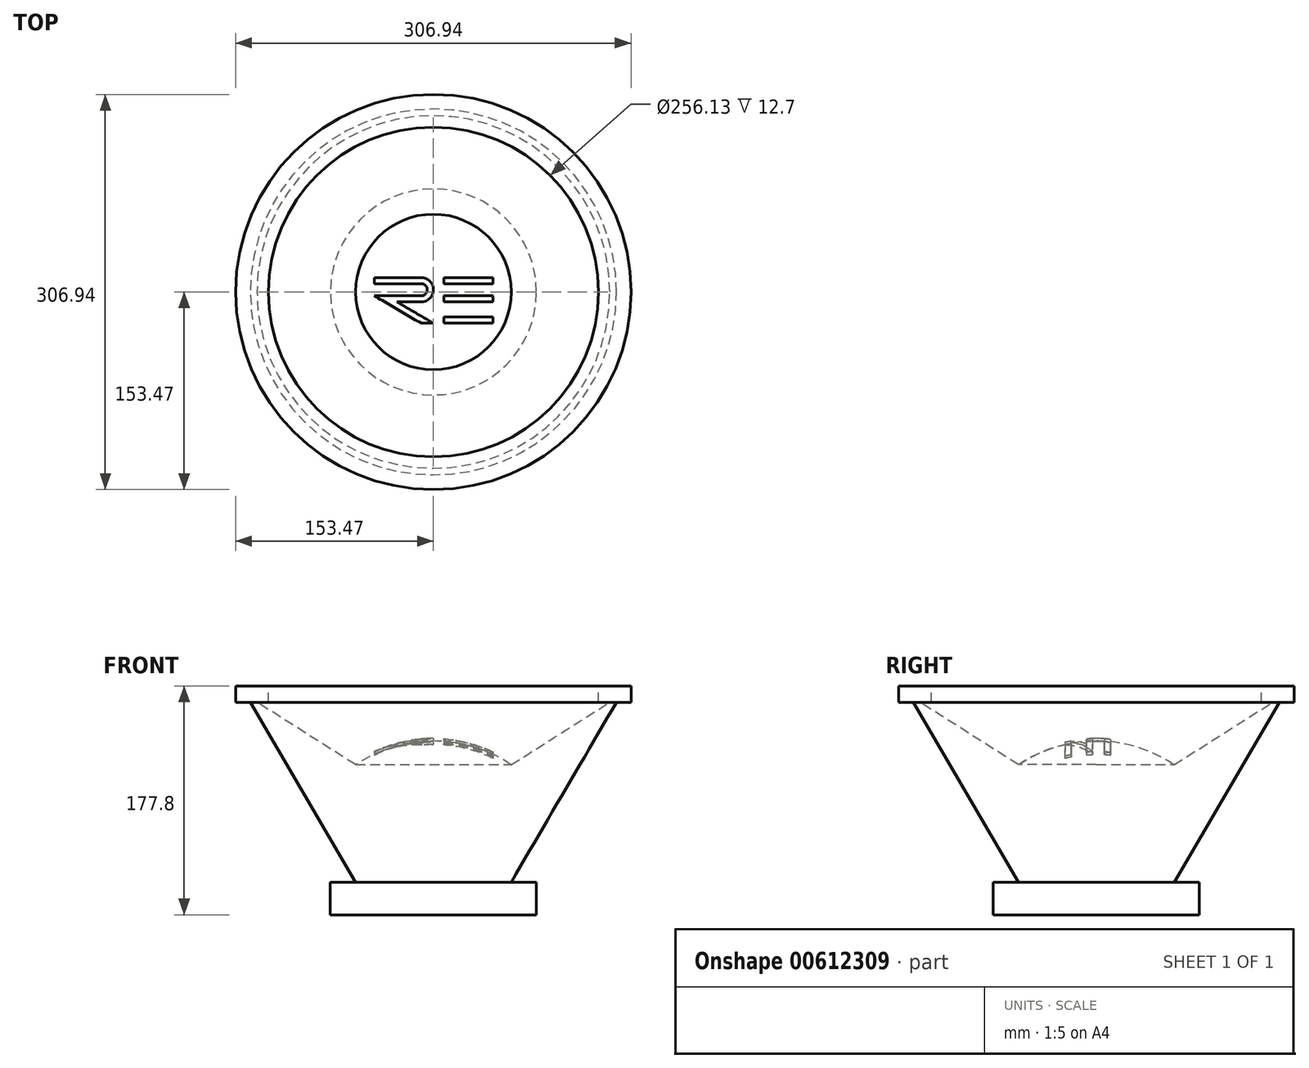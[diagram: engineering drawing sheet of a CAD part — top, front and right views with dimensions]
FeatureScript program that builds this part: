
annotation { "Feature Type Name" : "Feature", "Feature Type Description" : "" }
export const myFeature = defineFeature(function(context is Context, id is Id, definition is map)
    precondition{}
    {
        {
            var Q0;
            Q0=qCreatedBy(makeId("Right.planeOp"),FACE);
            var sketch = newSketch(context, id + "F0", { "sketchPlane" : qUnion([Q0])});
            skLineSegment(sketch, "E0", {"start": v(0, -91.62) * mm, "end": v(80.01, -91.62) * mm});
            skLineSegment(sketch, "E1", {"start": v(80.01, -91.62) * mm, "end": v(80.01, -66.22) * mm});
            skLineSegment(sketch, "E2", {"start": v(80.01, -66.22) * mm, "end": v(60.42, -66.22) * mm});
            skLineSegment(sketch, "E3", {"start": v(60.42, -66.22) * mm, "end": v(142.06, 73.48) * mm});
            skLineSegment(sketch, "E4", {"start": v(142.06, 73.48) * mm, "end": v(153.47, 73.48) * mm});
            skLineSegment(sketch, "E5", {"start": v(153.47, 73.48) * mm, "end": v(153.47, 86.18) * mm});
            skLineSegment(sketch, "E6", {"start": v(153.47, 86.18) * mm, "end": v(128.07, 86.18) * mm});
            skLineSegment(sketch, "E7", {"start": v(128.07, 86.18) * mm, "end": v(128.07, 73.48) * mm});
            skLineSegment(sketch, "E8", {"start": v(128.07, 73.48) * mm, "end": v(136.93, 73.48) * mm});
            skLineSegment(sketch, "E9", {"start": v(136.93, 73.48) * mm, "end": v(60.42, 24.96) * mm});
            skArc(sketch, "E10", {"start": v(60.42, 24.96) * mm, "mid": v(31.57, 38.63) * mm, "end": v(0, 43.39) * mm});
            skLineSegment(sketch, "E11", {"start": v(0, 43.39) * mm, "end": v(0, -91.62) * mm});
            skSolve(sketch);
        }
        {
            var Q0;
            Q0 = qSketchRegion(id + "F0", true);
            var Q1;
            Q1=sQuery(id+"F0.wireOp",EDGE,"E11");
            revolve(context, id + "F1", {"entities" : qUnion([Q0]), "axis" : qUnion([Q1]), "revolveType" : RevolveType.FULL});
        }
        {
            var Q0;
            Q0=qCreatedBy(makeId("Top.planeOp"),FACE);
            cPlane(context, id + "F2", {"entities" : qUnion([Q0]), "cplaneType" : CPlaneType.OFFSET, "offset" : 25.4 * mm, "width" : 152.4 * mm, "height" : 152.4 * mm});
        }
        {
            var Q0;
            Q0=qCreatedBy(id+"F2.planeOp",FACE);
            var sketch = newSketch(context, id + "F3", { "sketchPlane" : qUnion([Q0])});
            skLineSegment(sketch, "E12", {"start": v(-45.92, 11.17) * mm, "end": v(-9.42, 11.17) * mm});
            skArc(sketch, "E13", {"start": v(-9.42, -7.68) * mm, "mid": v(0, 1.74) * mm, "end": v(-9.42, 11.17) * mm});
            skLineSegment(sketch, "E14", {"start": v(-9.42, -7.68) * mm, "end": v(-28.38, -7.68) * mm});
            skLineSegment(sketch, "E15", {"start": v(-28.38, -7.68) * mm, "end": v(0, -24.3) * mm});
            skLineSegment(sketch, "E16", {"start": v(0, -24.3) * mm, "end": v(-9.42, -24.3) * mm});
            skLineSegment(sketch, "E17", {"start": v(-9.42, -24.3) * mm, "end": v(-45.92, -2.92) * mm});
            skLineSegment(sketch, "E18", {"start": v(-45.92, -2.92) * mm, "end": v(-9.42, -2.92) * mm});
            skArc(sketch, "E19", {"start": v(-9.42, -2.92) * mm, "mid": v(-4.76, 1.74) * mm, "end": v(-9.42, 6.4) * mm});
            skLineSegment(sketch, "E20", {"start": v(-9.42, 6.4) * mm, "end": v(-45.92, 6.4) * mm});
            skLineSegment(sketch, "E21", {"start": v(-45.92, 6.4) * mm, "end": v(-45.92, 11.17) * mm});
            skLineSegment(sketch, "E22", {"start": v(8.08, 11.17) * mm, "end": v(46.36, 11.17) * mm});
            skLineSegment(sketch, "E23", {"start": v(46.36, 11.17) * mm, "end": v(46.36, 6.4) * mm});
            skLineSegment(sketch, "E24", {"start": v(46.36, 6.4) * mm, "end": v(8.08, 6.4) * mm});
            skLineSegment(sketch, "E25", {"start": v(8.08, 6.4) * mm, "end": v(8.08, 11.17) * mm});
            skLineSegment(sketch, "E26", {"start": v(8.08, -2.92) * mm, "end": v(8.08, -7.68) * mm});
            skLineSegment(sketch, "E27", {"start": v(8.08, -7.68) * mm, "end": v(46.36, -7.68) * mm});
            skLineSegment(sketch, "E28", {"start": v(46.36, -7.68) * mm, "end": v(46.36, -2.92) * mm});
            skLineSegment(sketch, "E29", {"start": v(46.36, -2.92) * mm, "end": v(8.08, -2.92) * mm});
            skLineSegment(sketch, "E30", {"start": v(8.08, -24.3) * mm, "end": v(8.08, -19.55) * mm});
            skLineSegment(sketch, "E31", {"start": v(8.08, -19.55) * mm, "end": v(46.36, -19.55) * mm});
            skLineSegment(sketch, "E32", {"start": v(46.36, -19.55) * mm, "end": v(46.36, -24.3) * mm});
            skLineSegment(sketch, "E33", {"start": v(46.36, -24.3) * mm, "end": v(8.08, -24.3) * mm});
            skSolve(sketch);
        }
        {
            var Q0;
            Q0 = qSketchRegion(id + "F3", true);
            var Q1;
            Q1=makeQuery(id+"F1.opRevolve","SWEPT_FACE",FACE,{"disambiguationData":[OSD([sQuery(id+"F0.wireOp",EDGE,"E10")])]});
            var Q2;
            Q2=makeQuery(id+"F1.opRevolve","SWEPT_BODY",BODY,{"disambiguationData":[OSD([sQuery(id+"F0.wireOp",EDGE,"E0"),sQuery(id+"F0.wireOp",EDGE,"E1"),sQuery(id+"F0.wireOp",EDGE,"E2"),sQuery(id+"F0.wireOp",EDGE,"E3"),sQuery(id+"F0.wireOp",EDGE,"E4"),sQuery(id+"F0.wireOp",EDGE,"E5"),sQuery(id+"F0.wireOp",EDGE,"E6"),sQuery(id+"F0.wireOp",EDGE,"E7"),sQuery(id+"F0.wireOp",EDGE,"E8"),sQuery(id+"F0.wireOp",EDGE,"E9"),sQuery(id+"F0.wireOp",EDGE,"E10"),sQuery(id+"F0.wireOp",EDGE,"E11")])]});
            extrude(context, id + "F4", {"entities" : qUnion([Q0]), "operationType" : NewBodyOperationType.ADD, "endBound" : BoundingType.UP_TO_SURFACE, "depth" : 22.22 * mm, "endBoundEntityFace" : qUnion([Q1]), "endBoundEntityBody" : qUnion([Q2]), "hasOffset" : true, "offsetDistance" : 2.03 * mm, "offsetOppositeDirection" : true, "hasSecondDirectionOffset" : true, "secondDirectionOffsetDistance" : 2.03 * mm});
        }
    });
